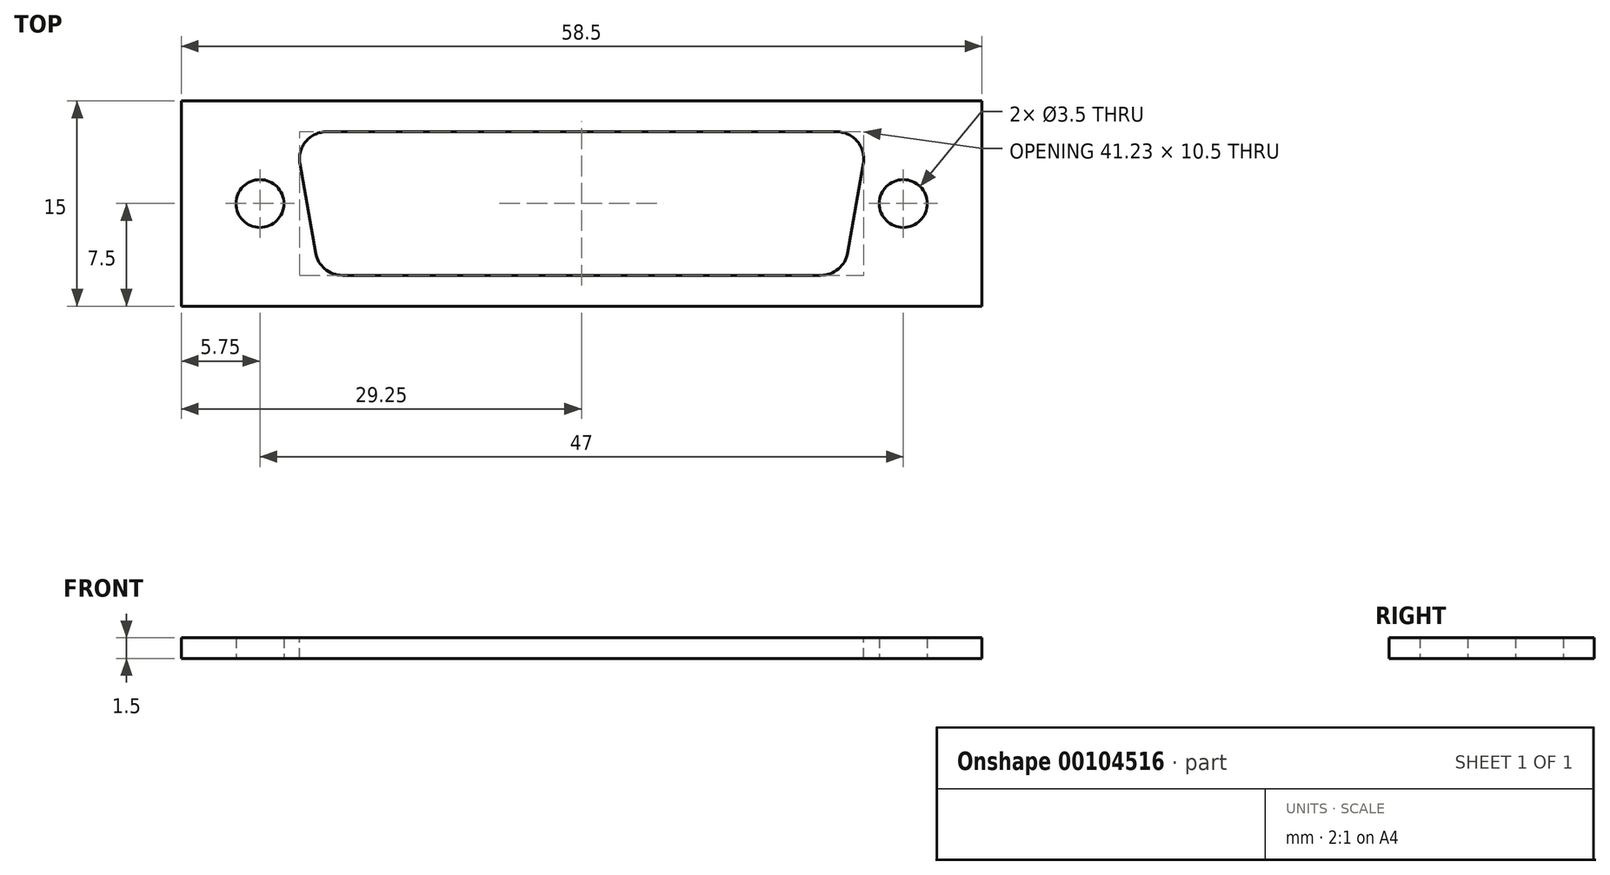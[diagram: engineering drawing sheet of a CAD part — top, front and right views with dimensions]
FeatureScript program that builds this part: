
annotation { "Feature Type Name" : "Feature", "Feature Type Description" : "" }
export const myFeature = defineFeature(function(context is Context, id is Id, definition is map)
    precondition{}
    {
        {
            var Q0;
            Q0=qCreatedBy(makeId("Top.planeOp"),FACE);
            var sketch = newSketch(context, id + "F0", { "sketchPlane" : qUnion([Q0])});
            skLineSegment(sketch, "E0.bottom", {"start": v(-29.25, -7.5) * mm, "end": v(29.25, -7.5) * mm});
            skLineSegment(sketch, "E0.top", {"start": v(-29.25, 7.5) * mm, "end": v(29.25, 7.5) * mm});
            skLineSegment(sketch, "E0.left", {"start": v(-29.25, -7.5) * mm, "end": v(-29.25, 7.5) * mm});
            skLineSegment(sketch, "E0.right", {"start": v(29.25, -7.5) * mm, "end": v(29.25, 7.5) * mm});
            skPoint(sketch, "E0.middle", {"position": v(0, 0) * mm});
            skPoint(sketch, "E0.middle.positionSnap0", {"position": v(-69.19, 4.04) * mm});
            skPoint(sketch, "E0.centerSnap0", {"position": v(-69.19, 4.04) * mm});
            skPoint(sketch, "E1", {"position": v(80.81, 4.04) * mm});
            skCircle(sketch, "E2", {"center": v(-23.5, 0) * mm, "radius": 1.75 * mm});
            skCircle(sketch, "E3", {"center": v(23.5, 0) * mm, "radius": 1.75 * mm});
            skLineSegment(sketch, "E4", {"start": v(-19.15, -5.25) * mm, "end": v(19.15, -5.25) * mm});
            skLineSegment(sketch, "E5", {"start": v(19.15, -5.25) * mm, "end": v(21, 5.25) * mm});
            skLineSegment(sketch, "E6", {"start": v(21, 5.25) * mm, "end": v(-21, 5.25) * mm});
            skLineSegment(sketch, "E7", {"start": v(-21, 5.25) * mm, "end": v(-19.15, -5.25) * mm});
            skPoint(sketch, "E8", {"position": v(0, 5.25) * mm});
            skPoint(sketch, "E9", {"position": v(29.25, 0) * mm});
            skSolve(sketch);
        }
        {
            var Q0;
            Q0=makeQuery(id+"F0.imprint","IMPRINT",FACE,{"disambiguationData":[TD([[makeQuery(id+"F0.imprint","IMPRINT",EDGE,{"derivedFrom":sQuery(id+"F0.wireOp",EDGE,"E0.bottom")}),1.0]])]});
            extrude(context, id + "F1", {"entities" : qUnion([Q0]), "depth" : 1.5 * mm});
        }
        {
            var Q0;
            Q0=makeQuery(id+"F1.opExtrude","SWEPT_EDGE",EDGE,{"disambiguationData":[OSD([sQuery(id+"F0.wireOp",EDGE,"E6"),sQuery(id+"F0.wireOp",EDGE,"E7")])]});
            var Q1;
            Q1=makeQuery(id+"F1.opExtrude","SWEPT_EDGE",EDGE,{"disambiguationData":[OSD([sQuery(id+"F0.wireOp",EDGE,"E4"),sQuery(id+"F0.wireOp",EDGE,"E7")])]});
            var Q2;
            Q2=makeQuery(id+"F1.opExtrude","SWEPT_EDGE",EDGE,{"disambiguationData":[OSD([sQuery(id+"F0.wireOp",EDGE,"E4"),sQuery(id+"F0.wireOp",EDGE,"E5")])]});
            var Q3;
            Q3=makeQuery(id+"F1.opExtrude","SWEPT_EDGE",EDGE,{"disambiguationData":[OSD([sQuery(id+"F0.wireOp",EDGE,"E5"),sQuery(id+"F0.wireOp",EDGE,"E6")])]});
            fillet(context, id + "F2", {"entities" : qUnion([Q0, Q1, Q2, Q3]), "radius" : 2 * mm, "tangentPropagation" : true, "allowEdgeOverflow" : false});
        }
    });
